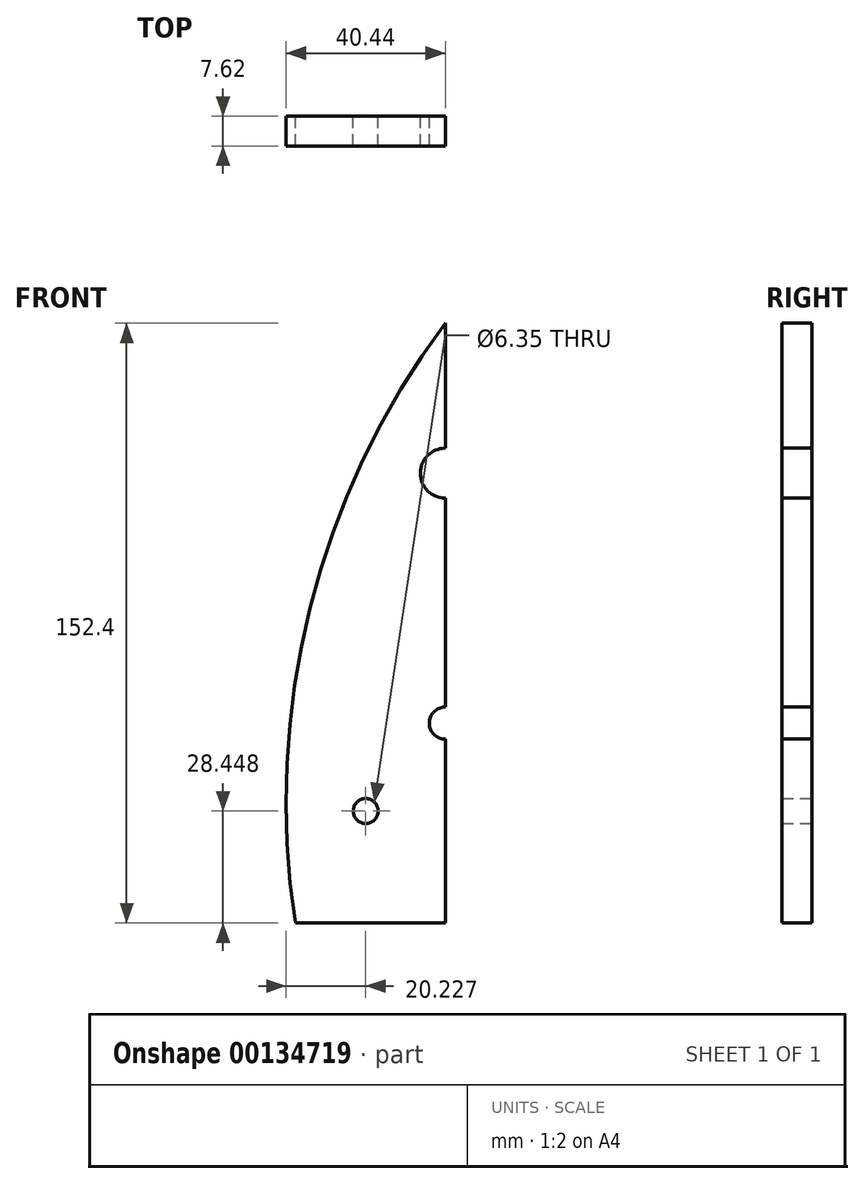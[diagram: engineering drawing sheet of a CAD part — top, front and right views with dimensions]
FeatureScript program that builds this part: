
annotation { "Feature Type Name" : "Feature", "Feature Type Description" : "" }
export const myFeature = defineFeature(function(context is Context, id is Id, definition is map)
    precondition{}
    {
        {
            var Q0;
            Q0=qCreatedBy(makeId("Front.planeOp"),FACE);
            var sketch = newSketch(context, id + "F0", { "sketchPlane" : qUnion([Q0])});
            skLineSegment(sketch, "E0", {"start": v(0, 101.6) * mm, "end": v(0, -50.8) * mm});
            skLineSegment(sketch, "E1", {"start": v(-38.1, -50.8) * mm, "end": v(38.1, -50.8) * mm});
            skArc(sketch, "E2", {"start": v(0, 101.6) * mm, "mid": v(-34.37, 29.23) * mm, "end": v(-38.1, -50.8) * mm});
            skArc(sketch, "E3.MirrorCS", {"start": v(0, 101.6) * mm, "mid": v(34.37, 29.23) * mm, "end": v(38.1, -50.8) * mm});
            skCircle(sketch, "E4", {"center": v(0, 63.5) * mm, "radius": 6.35 * mm});
            skCircle(sketch, "E5", {"center": v(0, 0) * mm, "radius": 4.06 * mm});
            skLineSegment(sketch, "E6", {"start": v(0, 0) * mm, "end": v(0, -22.35) * mm, "construction": true});
            skLineSegment(sketch, "E7", {"start": v(-40.43, -22.35) * mm, "end": v(40.43, -22.35) * mm, "construction": true});
            skLineSegment(sketch, "E8", {"start": v(-40.43, -22.35) * mm, "end": v(0, -22.35) * mm, "construction": true});
            skPoint(sketch, "E9", {"position": v(-20.21, -22.35) * mm});
            skCircle(sketch, "E10", {"center": v(-20.21, -22.35) * mm, "radius": 3.18 * mm});
            skSolve(sketch);
        }
        {
            var Q0;
            {var subQ0=sQuery(id+"F0.wireOp",EDGE,"E2");Q0=makeQuery(id+"F0.imprint","IMPRINT",FACE,{"disambiguationData":[TD([[makeQuery(id+"F0.imprint","IMPRINT",EDGE,{"derivedFrom":subQ0}),1.0]])]});}
            var Q1;
            {var subQ0=sQuery(id+"F0.wireOp",EDGE,"E3.MirrorCS");Q1=makeQuery(id+"F0.imprint","IMPRINT",FACE,{"disambiguationData":[TD([[makeQuery(id+"F0.imprint","IMPRINT",EDGE,{"derivedFrom":subQ0}),-1.0]])]});}
            extrude(context, id + "F1", {"entities" : qUnion([Q0, Q1]), "depth" : 7.62 * mm});
        }
    });
